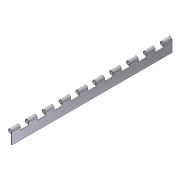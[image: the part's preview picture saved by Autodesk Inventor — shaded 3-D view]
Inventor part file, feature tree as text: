
AUTODESK INVENTOR PART (.ipt)
format: ipt  version: 2012 (Build 160160000, 160)  size: 138,752 bytes
history: native  units: in
note: dims shown in document units (in); Inventor stores cm internally (conversion verified against a paired STEP export)
features: extrude x2, sketch x2, fillet x1, pattern_linear x1, projected_geometry x1
ambient origin geometry x8: Origin, YZ Plane, XZ Plane, XY Plane, X Axis, Y Axis, Z Axis, Center Point
bodies: Solid1 (feature_tree)
feature tree (7):
  extrude  "Extrusion1"  Depth=0.09in
  extrude  "Extrusion2"  Depth=16.0in TaperAngle=0.0deg
  fillet  "Fillet1"  Radius=1.0in
  pattern_linear  "Rectangular Pattern1"  Spacing1=1.0in  [1 undecoded]
  sketch  "Sketch1"  dims[d0=0.445in d1=0.09in]
  sketch  "Sketch2"  dims[d2=0.09in d3=16.0in d4=0.0in d5=1.0in d6=1.0in d7=0.125in d8=16.0in d9=0.0in d10=0.125in d11=3.1496in d13=2.0in]
  projected_geometry  "Projected Loop1"
note: 1 required parameter value undecoded (feature->parameter linkage not recoverable at this tier; creation-order binding heuristic only, values carry confidence <= 0.55)
